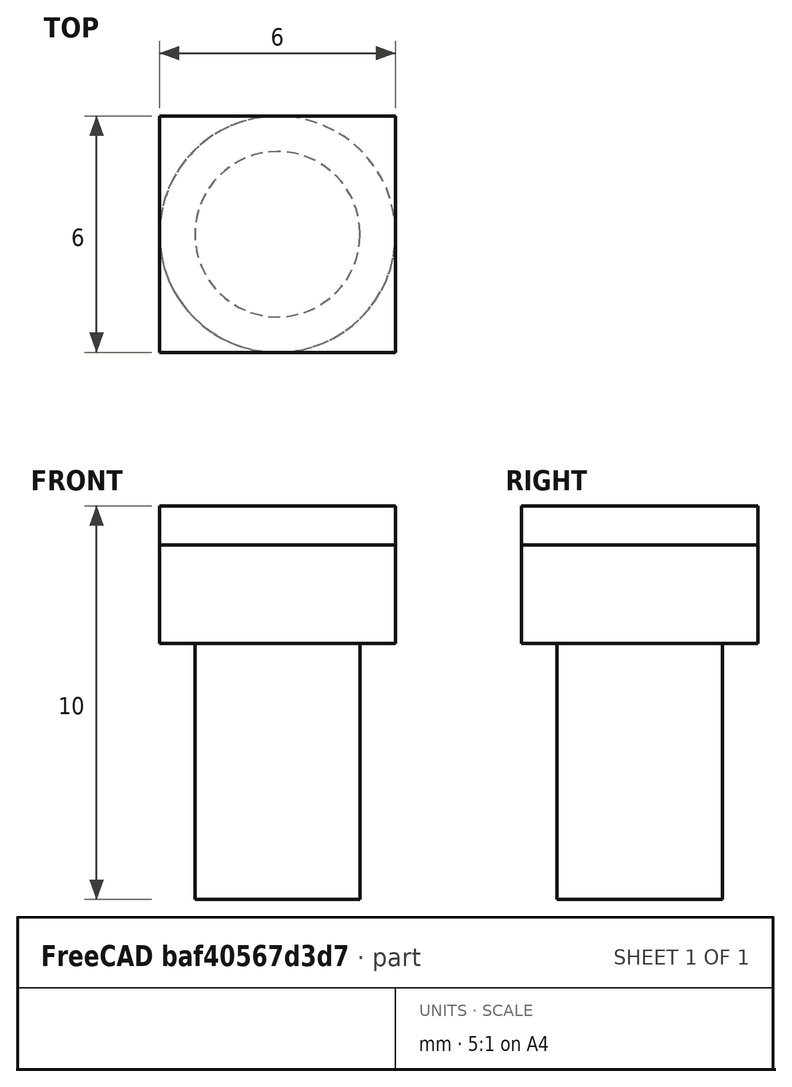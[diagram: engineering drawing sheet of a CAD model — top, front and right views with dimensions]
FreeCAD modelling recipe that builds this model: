
FCSTD DOCUMENT  (FreeCAD 0.17R13522 (Git))
Label: perforador_led_3mm
License: CreativeCommons Attribution-ShareAlike
LicenseURL: http://creativecommons.org/licenses/by-sa/4.0/
objects: Part::Part2DObjectPython×2, Part::Extrusion×2, Part::Fuse×2, Part::Box×1, Part::Feature×1
note: 8 computed .brp shape members not serialized (recipe doc carries the construction recipe); baked Part::Feature solids carry a one-line shape summary decoded from their .brp

FEATURE [Part::Box] Box  label="Cube"
  AttacherType = Attacher::AttachEngine3D
  Height = 1
  Length = 6
  Width = 6
FEATURE [Part::Part2DObjectPython] Circle  label="circulo exterior"  # Draft 2D object (typed FeaturePython)
  FirstAngle = 0
  LastAngle = 0
  MakeFace = true
  Placement = pos=(3,3,1) rot=(0,0,1;3.14159rad)
  Radius = 3
FEATURE [Part::Part2DObjectPython] Circle001  label="circulo interior"  # Draft 2D object (typed FeaturePython)
  FirstAngle = 0
  LastAngle = 0
  MakeFace = true
  Placement = pos=(3,3,1) rot=(0,0,1;3.14159rad)
  Radius = 2.1
FEATURE [Part::Extrusion] Extrude
  Base = -> Circle001
  Dir = (0,0,1)
  DirMode = 2
  FaceMakerClass = Part::FaceMakerBullseye
  LengthFwd = 10
  LengthRev = 0
  Placement = pos=(0,0,-10) rot=(0,0,1;0rad)
  Solid = false
  Symmetric = false
FEATURE [Part::Extrusion] Extrude001
  Base = -> Circle
  Dir = (0,0,1)
  DirMode = 2
  FaceMakerClass = Part::FaceMakerBullseye
  LengthFwd = 3.5
  LengthRev = 0
  Placement = pos=(0,0,-3.5) rot=(0,0,1;0rad)
  Solid = false
  Symmetric = false
FEATURE [Part::Fuse] Fusion
  Base = -> Extrude
  Refine = true
  Tool = -> Extrude001
FEATURE [Part::Fuse] Fusion001  label="perforador led 3 mm"
  Base = -> Box
  Refine = true
  Tool = -> Fusion
FEATURE [Part::Feature] Fusion001001  label="perforador led 3 mm001"
  shape: bbox 6 x 6 x 10 mm, 13 faces (baked)
